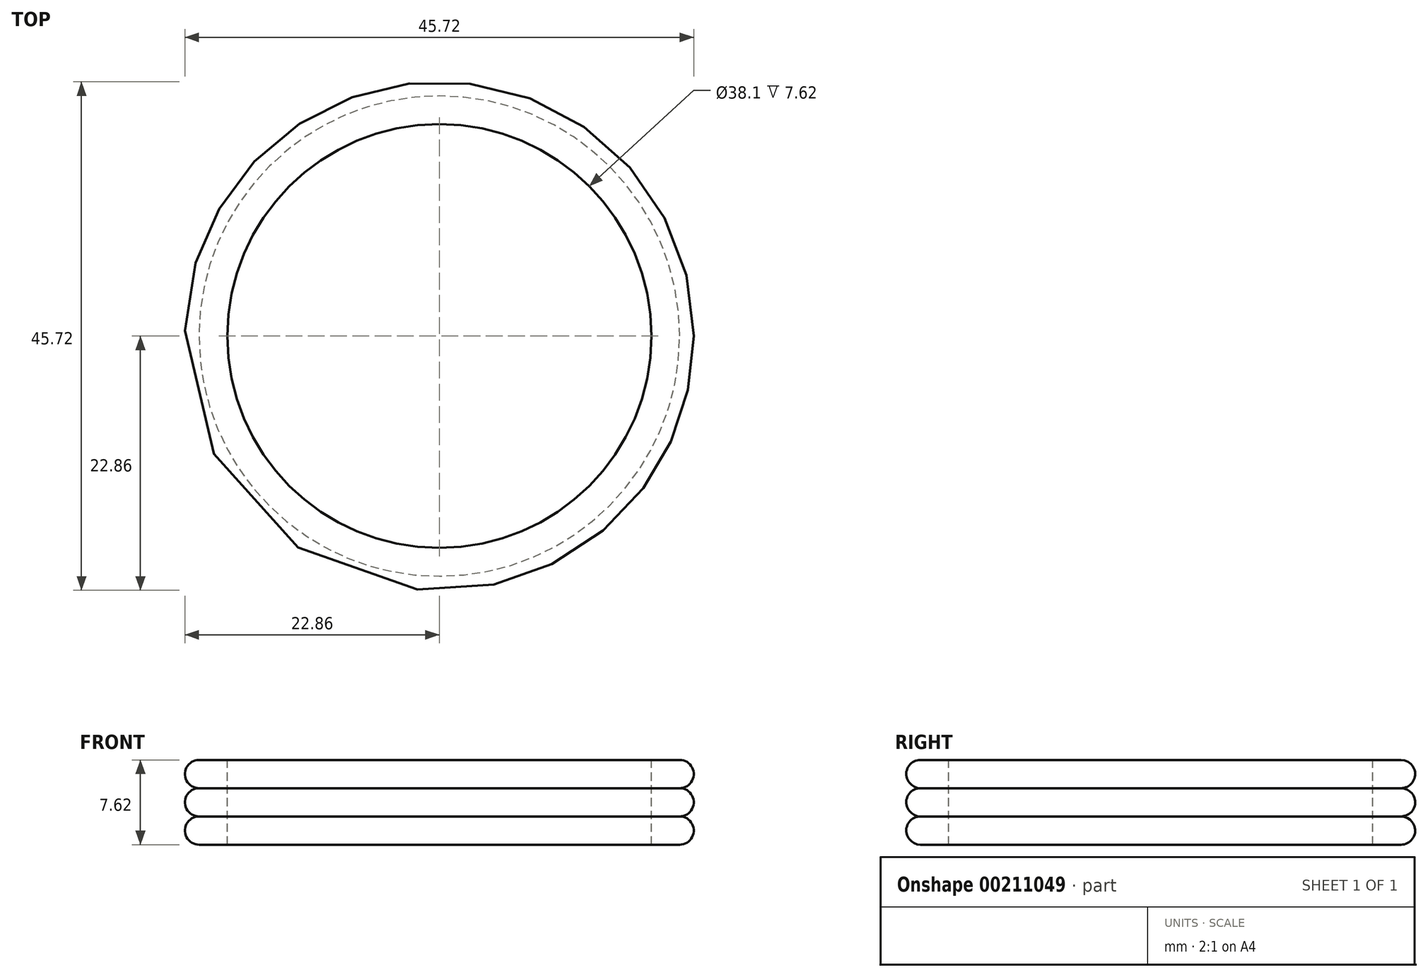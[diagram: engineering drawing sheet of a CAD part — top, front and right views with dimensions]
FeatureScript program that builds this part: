
annotation { "Feature Type Name" : "Feature", "Feature Type Description" : "" }
export const myFeature = defineFeature(function(context is Context, id is Id, definition is map)
    precondition{}
    {
        {
            var Q0;
            Q0=qCreatedBy(makeId("Front.planeOp"),FACE);
            var sketch = newSketch(context, id + "F0", { "sketchPlane" : qUnion([Q0])});
            skLineSegment(sketch, "E0", {"start": v(19.05, 3.81) * mm, "end": v(19.05, -3.81) * mm});
            skLineSegment(sketch, "E1", {"start": v(19.05, -3.81) * mm, "end": v(21.59, -3.81) * mm});
            skArc(sketch, "E2", {"start": v(21.59, -3.81) * mm, "mid": v(22.86, -2.54) * mm, "end": v(21.59, -1.27) * mm});
            skArc(sketch, "E3", {"start": v(21.59, -1.27) * mm, "mid": v(22.86, 0) * mm, "end": v(21.59, 1.27) * mm});
            skArc(sketch, "E4", {"start": v(21.59, 1.27) * mm, "mid": v(22.86, 2.54) * mm, "end": v(21.59, 3.8) * mm});
            skLineSegment(sketch, "E5", {"start": v(19.05, 3.8) * mm, "end": v(21.59, 3.8) * mm});
            skLineSegment(sketch, "E6", {"start": v(0, 11.55) * mm, "end": v(0, -4.98) * mm, "construction": true});
            skSolve(sketch);
        }
        {
            var Q0;
            Q0=makeQuery(id+"F0.imprint","IMPRINT",FACE,{"disambiguationData":[TD([[makeQuery(id+"F0.imprint","IMPRINT",EDGE,{"derivedFrom":sQuery(id+"F0.wireOp",EDGE,"E0")}),1.0]])]});
            var Q1;
            Q1=sQuery(id+"F0.wireOp",EDGE,"E6");
            revolve(context, id + "F1", {"entities" : qUnion([Q0]), "axis" : qUnion([Q1]), "revolveType" : RevolveType.FULL});
        }
    });
